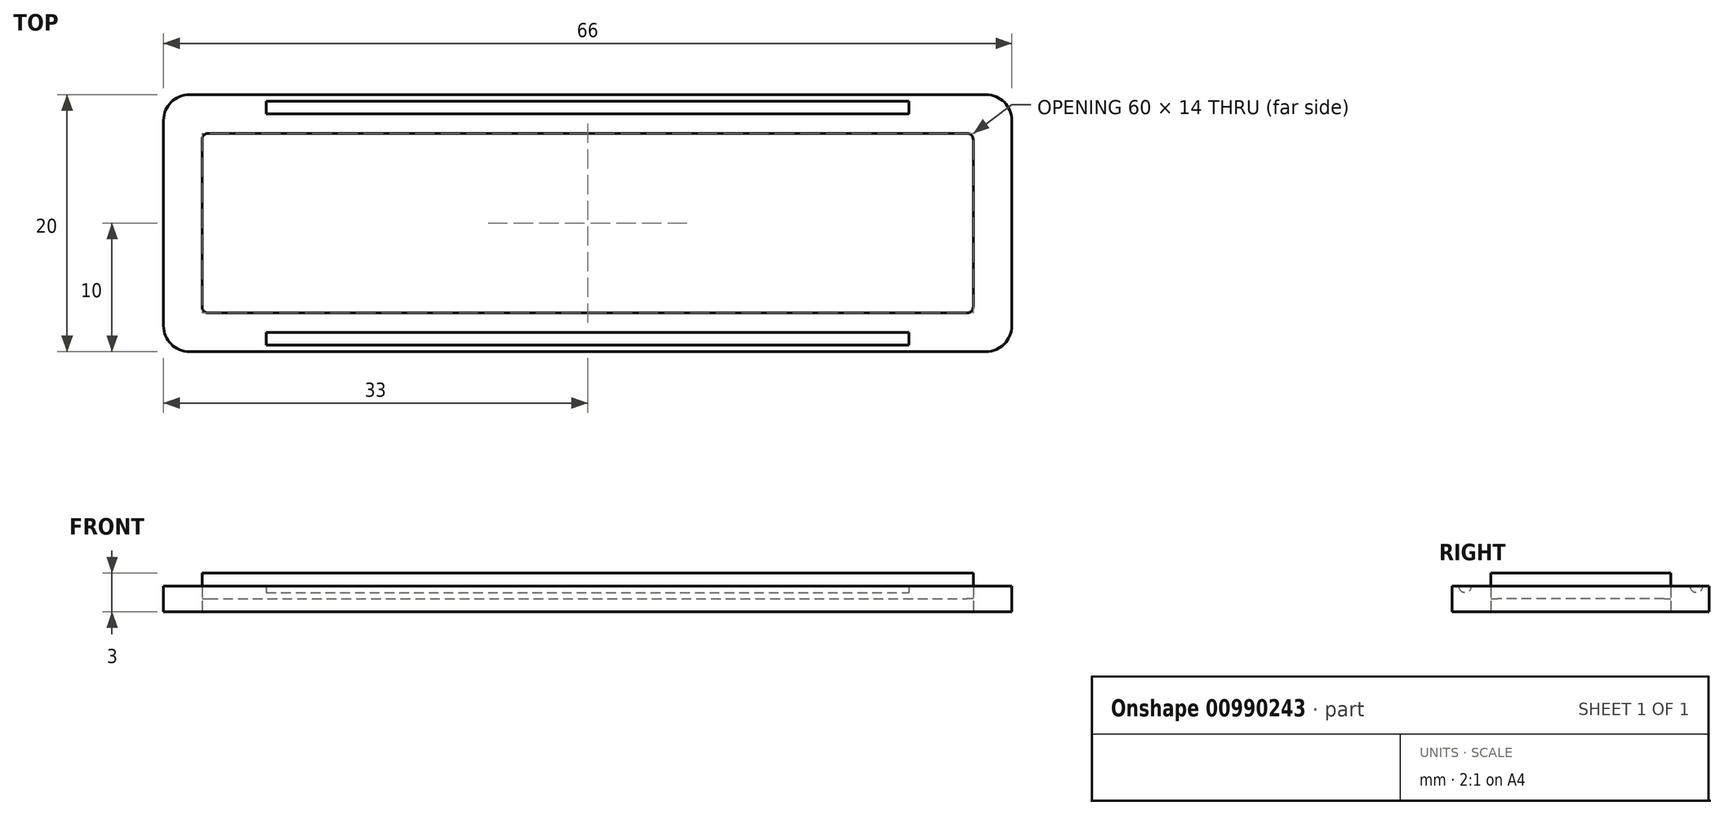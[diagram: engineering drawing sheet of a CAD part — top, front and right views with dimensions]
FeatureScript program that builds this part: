
annotation { "Feature Type Name" : "Feature", "Feature Type Description" : "" }
export const myFeature = defineFeature(function(context is Context, id is Id, definition is map)
    precondition{}
    {
        {
            var Q0;
            Q0=qCreatedBy(makeId("Top.planeOp"),FACE);
            var sketch = newSketch(context, id + "F0", { "sketchPlane" : qUnion([Q0])});
            skLineSegment(sketch, "E0.bottom", {"start": v(-30, 7) * mm, "end": v(30, 7) * mm});
            skLineSegment(sketch, "E0.top", {"start": v(-30, -7) * mm, "end": v(30, -7) * mm});
            skLineSegment(sketch, "E0.left", {"start": v(-30, 7) * mm, "end": v(-30, -7) * mm});
            skLineSegment(sketch, "E0.right", {"start": v(30, 7) * mm, "end": v(30, -7) * mm});
            skPoint(sketch, "E0.middle", {"position": v(0, 0) * mm});
            skLineSegment(sketch, "E1.bottom", {"start": v(-31, 10) * mm, "end": v(31, 10) * mm});
            skLineSegment(sketch, "E1.top", {"start": v(-31, -10) * mm, "end": v(31, -10) * mm});
            skLineSegment(sketch, "E1.left", {"start": v(-33, 8) * mm, "end": v(-33, -8) * mm});
            skLineSegment(sketch, "E1.right", {"start": v(33, 8) * mm, "end": v(33, -8) * mm});
            skPoint(sketch, "E2.visualSharp", {"position": v(33, 10) * mm});
            skArc(sketch, "E2.filletArc", {"start": v(33, 8) * mm, "mid": v(32.41, 9.41) * mm, "end": v(31, 10) * mm});
            skPoint(sketch, "E3.visualSharp", {"position": v(-33, 10) * mm});
            skArc(sketch, "E3.filletArc", {"start": v(-31, 10) * mm, "mid": v(-32.41, 9.41) * mm, "end": v(-33, 8) * mm});
            skPoint(sketch, "E4.visualSharp", {"position": v(-33, -10) * mm});
            skArc(sketch, "E4.filletArc", {"start": v(-33, -8) * mm, "mid": v(-32.41, -9.41) * mm, "end": v(-31, -10) * mm});
            skPoint(sketch, "E5.visualSharp", {"position": v(33, -10) * mm});
            skArc(sketch, "E5.filletArc", {"start": v(31, -10) * mm, "mid": v(32.41, -9.41) * mm, "end": v(33, -8) * mm});
            skSolve(sketch);
        }
        {
            var Q0;
            Q0 = qSketchRegion(id + "F0", true);
            extrude(context, id + "F1", {"entities" : qUnion([Q0]), "depth" : 2 * mm, "offsetDistance" : 25 * mm});
        }
        {
            var Q0;
            Q0=makeQuery(id+"F1.opExtrude","CAP_FACE",FACE,{"disambiguationData":[OSD([sQuery(id+"F0.wireOp",EDGE,"E0.bottom"),sQuery(id+"F0.wireOp",EDGE,"E0.top"),sQuery(id+"F0.wireOp",EDGE,"E0.left"),sQuery(id+"F0.wireOp",EDGE,"E0.right"),sQuery(id+"F0.wireOp",EDGE,"E1.bottom"),sQuery(id+"F0.wireOp",EDGE,"E1.top"),sQuery(id+"F0.wireOp",EDGE,"E1.left"),sQuery(id+"F0.wireOp",EDGE,"E1.right"),sQuery(id+"F0.wireOp",EDGE,"E2.filletArc"),sQuery(id+"F0.wireOp",EDGE,"E3.filletArc"),sQuery(id+"F0.wireOp",EDGE,"E4.filletArc"),sQuery(id+"F0.wireOp",EDGE,"E5.filletArc")])],"isStart":false});
            var sketch = newSketch(context, id + "F2", { "sketchPlane" : qUnion([Q0])});
            skLineSegment(sketch, "E6.0", {"start": v(-30, 7) * mm, "end": v(30, 7) * mm});
            skLineSegment(sketch, "E7.0", {"start": v(-30, 7) * mm, "end": v(-30, -7) * mm});
            skLineSegment(sketch, "E8.0", {"start": v(-30, -7) * mm, "end": v(30, -7) * mm});
            skLineSegment(sketch, "E9.0", {"start": v(30, 7) * mm, "end": v(30, -7) * mm});
            skSolve(sketch);
        }
        {
            var Q0;
            Q0 = qSketchRegion(id + "F2", true);
            extrude(context, id + "F3", {"entities" : qUnion([Q0]), "depth" : 1 * mm, "offsetDistance" : 25 * mm, "hasSecondDirection" : true, "secondDirectionOppositeDirection" : true, "secondDirectionDepth" : 1 * mm});
        }
        {
            var Q0;
            Q0=makeQuery(id+"F3.opExtrude","SWEPT_EDGE",EDGE,{"disambiguationData":[OSD([sQuery(id+"F2.wireOp",EDGE,"E6.0"),sQuery(id+"F2.wireOp",EDGE,"E7.0")])]});
            var Q1;
            Q1=makeQuery(id+"F3.opExtrude","SWEPT_EDGE",EDGE,{"disambiguationData":[OSD([sQuery(id+"F2.wireOp",EDGE,"E7.0"),sQuery(id+"F2.wireOp",EDGE,"E8.0")])]});
            var Q2;
            Q2=makeQuery(id+"F3.opExtrude","SWEPT_EDGE",EDGE,{"disambiguationData":[OSD([sQuery(id+"F2.wireOp",EDGE,"E8.0"),sQuery(id+"F2.wireOp",EDGE,"E9.0")])]});
            var Q3;
            Q3=makeQuery(id+"F3.opExtrude","SWEPT_EDGE",EDGE,{"disambiguationData":[OSD([sQuery(id+"F2.wireOp",EDGE,"E6.0"),sQuery(id+"F2.wireOp",EDGE,"E9.0")])]});
            fillet(context, id + "F4", {"entities" : qUnion([Q0, Q1, Q2, Q3]), "radius" : 0.5 * mm, "tangentPropagation" : true, "allowEdgeOverflow" : false});
        }
        {
            var Q0;
            Q0=qCreatedBy(makeId("Right.planeOp"),FACE);
            var sketch = newSketch(context, id + "F5", { "sketchPlane" : qUnion([Q0])});
            skLineSegment(sketch, "E10", {"start": v(-9.5, 2) * mm, "end": v(-8.5, 2) * mm});
            skArc(sketch, "E11", {"start": v(-9.5, 2) * mm, "mid": v(-9, 1.5) * mm, "end": v(-8.5, 2) * mm});
            skLineSegment(sketch, "E12", {"start": v(-10, 2.03) * mm, "end": v(-8, 2.03) * mm, "construction": true});
            skLineSegment(sketch, "E13", {"start": v(-9, 2.03) * mm, "end": v(-9, 3.61) * mm, "construction": true});
            skLineSegment(sketch, "E14", {"start": v(0, 0) * mm, "end": v(0, 5.81) * mm, "construction": true});
            skArc(sketch, "E15.MirrorCS", {"start": v(9.5, 2) * mm, "mid": v(9, 1.5) * mm, "end": v(8.5, 2) * mm});
            skLineSegment(sketch, "E16.MirrorCS", {"start": v(9.5, 2) * mm, "end": v(8.5, 2) * mm});
            skSolve(sketch);
        }
        {
            var Q0;
            Q0 = qSketchRegion(id + "F5", true);
            extrude(context, id + "F6", {"entities" : qUnion([Q0]), "operationType" : NewBodyOperationType.REMOVE, "endBound" : BoundingType.SYMMETRIC, "oppositeDirection" : true, "depth" : 50 * mm, "offsetDistance" : 25 * mm});
        }
        {
            var Q0;
            Q0=makeQuery(id+"F1.opExtrude","SWEPT_EDGE",EDGE,{"disambiguationData":[OSD([sQuery(id+"F0.wireOp",EDGE,"E0.top"),sQuery(id+"F0.wireOp",EDGE,"E0.right")])]});
            var Q1;
            Q1=makeQuery(id+"F1.opExtrude","SWEPT_EDGE",EDGE,{"disambiguationData":[OSD([sQuery(id+"F0.wireOp",EDGE,"E0.bottom"),sQuery(id+"F0.wireOp",EDGE,"E0.right")])]});
            var Q2;
            Q2=makeQuery(id+"F1.opExtrude","SWEPT_EDGE",EDGE,{"disambiguationData":[OSD([sQuery(id+"F0.wireOp",EDGE,"E0.top"),sQuery(id+"F0.wireOp",EDGE,"E0.left")])]});
            var Q3;
            Q3=makeQuery(id+"F1.opExtrude","SWEPT_EDGE",EDGE,{"disambiguationData":[OSD([sQuery(id+"F0.wireOp",EDGE,"E0.bottom"),sQuery(id+"F0.wireOp",EDGE,"E0.left")])]});
            fillet(context, id + "F7", {"entities" : qUnion([Q0, Q1, Q2, Q3]), "radius" : 0.5 * mm, "tangentPropagation" : true, "allowEdgeOverflow" : false});
        }
    });
